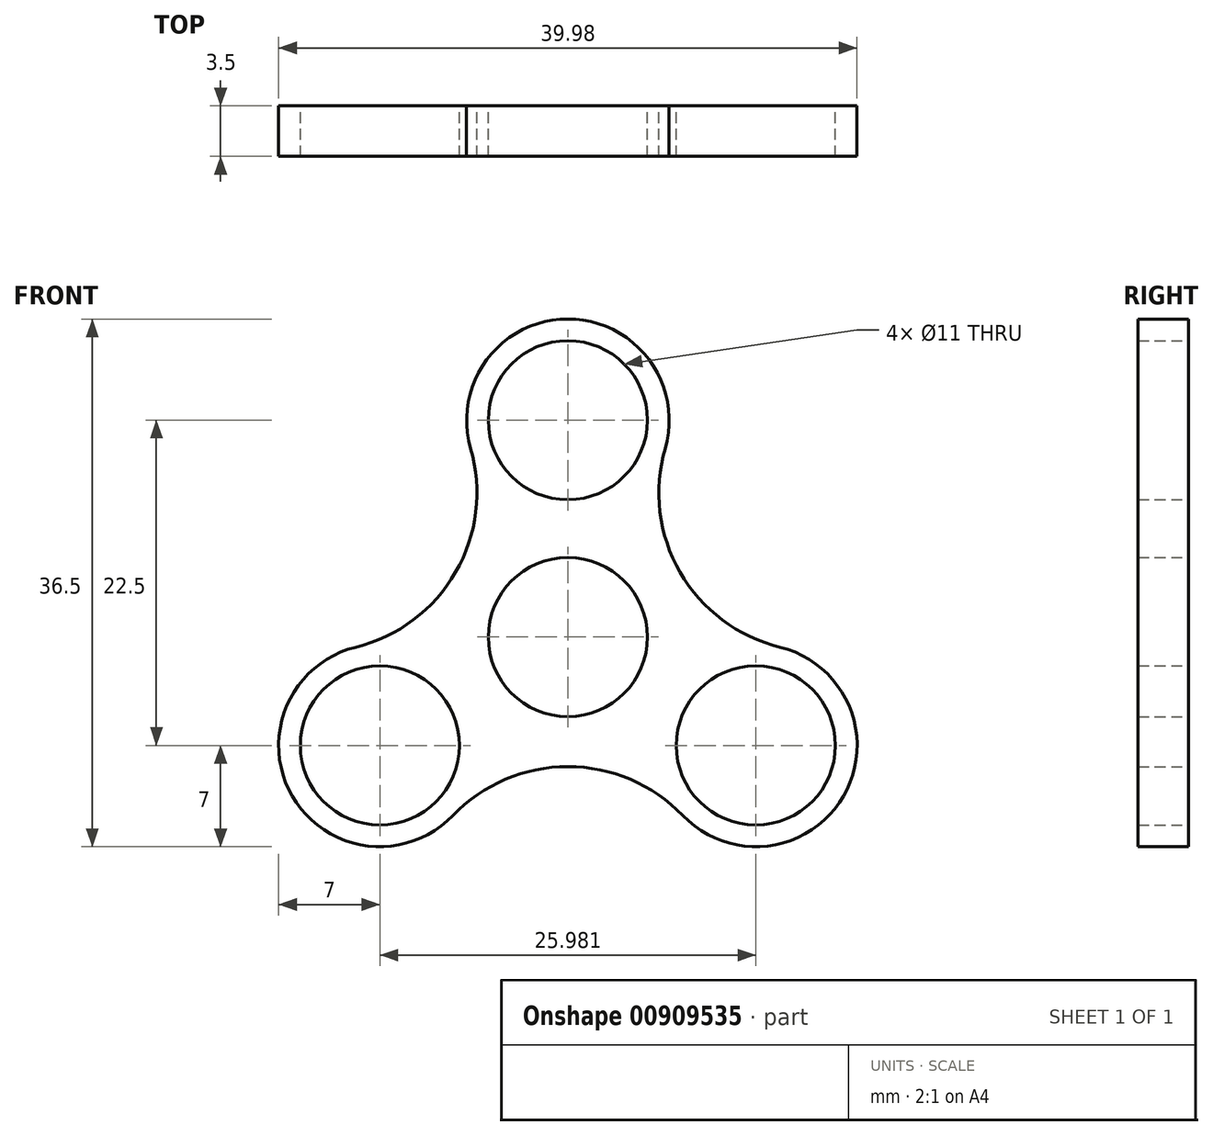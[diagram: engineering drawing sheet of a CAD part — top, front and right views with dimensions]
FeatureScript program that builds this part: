
annotation { "Feature Type Name" : "Feature", "Feature Type Description" : "" }
export const myFeature = defineFeature(function(context is Context, id is Id, definition is map)
    precondition{}
    {
        {
            var Q0;
            Q0=qCreatedBy(makeId("Front.planeOp"),FACE);
            var sketch = newSketch(context, id + "F0", { "sketchPlane" : qUnion([Q0])});
            skCircle(sketch, "E0", {"center": v(0, 0) * mm, "radius": 11 * mm});
            skCircle(sketch, "E1.cCircle", {"center": v(0, 0) * mm, "radius": 30 * mm, "construction": true});
            skLineSegment(sketch, "E1.0", {"start": v(0, 30) * mm, "end": v(25.98, -15) * mm, "construction": true});
            skLineSegment(sketch, "E1.1", {"start": v(25.98, -15) * mm, "end": v(-25.98, -15) * mm, "construction": true});
            skLineSegment(sketch, "E1.2", {"start": v(-25.98, -15) * mm, "end": v(0, 30) * mm, "construction": true});
            skArc(sketch, "E2", {"start": v(10.56, 26.93) * mm, "mid": v(0, 41) * mm, "end": v(-10.56, 26.93) * mm});
            skArc(sketch, "E3", {"start": v(-28.6, -4.32) * mm, "mid": v(-35.5, -20.5) * mm, "end": v(-18.04, -22.61) * mm});
            skArc(sketch, "E4", {"start": v(18.04, -22.61) * mm, "mid": v(35.5, -20.5) * mm, "end": v(28.6, -4.32) * mm});
            skArc(sketch, "E5", {"start": v(-28.6, -4.32) * mm, "mid": v(-12.92, 7.46) * mm, "end": v(-10.56, 26.93) * mm});
            skArc(sketch, "E6", {"start": v(18.04, -22.61) * mm, "mid": v(0, -14.92) * mm, "end": v(-18.04, -22.61) * mm});
            skArc(sketch, "E7", {"start": v(10.56, 26.93) * mm, "mid": v(12.92, 7.46) * mm, "end": v(28.6, -4.32) * mm});
            skArc(sketch, "E8.0", {"start": v(13.44, 26.1) * mm, "mid": v(15.52, 8.96) * mm, "end": v(29.32, -1.4) * mm});
            skArc(sketch, "E8.1", {"start": v(-29.32, -1.4) * mm, "mid": v(-15.52, 8.96) * mm, "end": v(-13.44, 26.1) * mm});
            skArc(sketch, "E8.2", {"start": v(-29.32, -1.4) * mm, "mid": v(-38.1, -22) * mm, "end": v(-15.88, -24.7) * mm});
            skArc(sketch, "E8.3", {"start": v(13.44, 26.1) * mm, "mid": v(0, 44) * mm, "end": v(-13.44, 26.1) * mm});
            skArc(sketch, "E8.4", {"start": v(15.88, -24.7) * mm, "mid": v(0, -17.92) * mm, "end": v(-15.88, -24.7) * mm});
            skArc(sketch, "E8.5", {"start": v(15.88, -24.7) * mm, "mid": v(38.1, -22) * mm, "end": v(29.32, -1.4) * mm});
            skCircle(sketch, "E9", {"center": v(-25.98, -15) * mm, "radius": 11 * mm});
            skCircle(sketch, "E10", {"center": v(25.98, -15) * mm, "radius": 11 * mm});
            skCircle(sketch, "E11", {"center": v(0, 30) * mm, "radius": 11 * mm});
            skSolve(sketch);
        }
        {
            var Q0;
            Q0=makeQuery(id+"F0.imprint","IMPRINT",FACE,{"disambiguationData":[TD([[makeQuery(id+"F0.imprint","IMPRINT",EDGE,{"derivedFrom":sQuery(id+"F0.wireOp",EDGE,"E0")}),-1.0]])]});
            var Q1;
            {var subQ1=sQuery(id+"F0.wireOp",EDGE,"E5");Q1=makeQuery(id+"F0.imprint","IMPRINT",FACE,{"disambiguationData":[TD([[makeQuery(id+"F0.imprint","IMPRINT",EDGE,{"derivedFrom":subQ1}),1.0]])]});}
            extrude(context, id + "F1", {"entities" : qUnion([Q0, Q1]), "depth" : 7 * mm, "offsetDistance" : 25 * mm});
        }
        {
            var Q0;
            Q0=makeQuery(id+"F1.opExtrude","SWEPT_BODY",BODY,{"disambiguationData":[OSD([sQuery(id+"F0.wireOp",EDGE,"E0"),sQuery(id+"F0.wireOp",EDGE,"E8.0"),sQuery(id+"F0.wireOp",EDGE,"E8.1"),sQuery(id+"F0.wireOp",EDGE,"E8.2"),sQuery(id+"F0.wireOp",EDGE,"E8.3"),sQuery(id+"F0.wireOp",EDGE,"E8.4"),sQuery(id+"F0.wireOp",EDGE,"E8.5"),sQuery(id+"F0.wireOp",EDGE,"E9"),sQuery(id+"F0.wireOp",EDGE,"E10"),sQuery(id+"F0.wireOp",EDGE,"E11")])]});
            var Q1;
            Q1=qCreatedBy(makeId("Origin.pointOp"),VERTEX);
            transform(context, id + "F2", {"entities" : qUnion([Q0]), "transformType" : TransformType.SCALE_UNIFORMLY, "scale" : 1 / 2, "scalePoint" : qUnion([Q1]), "makeCopy" : false});
        }
    });
